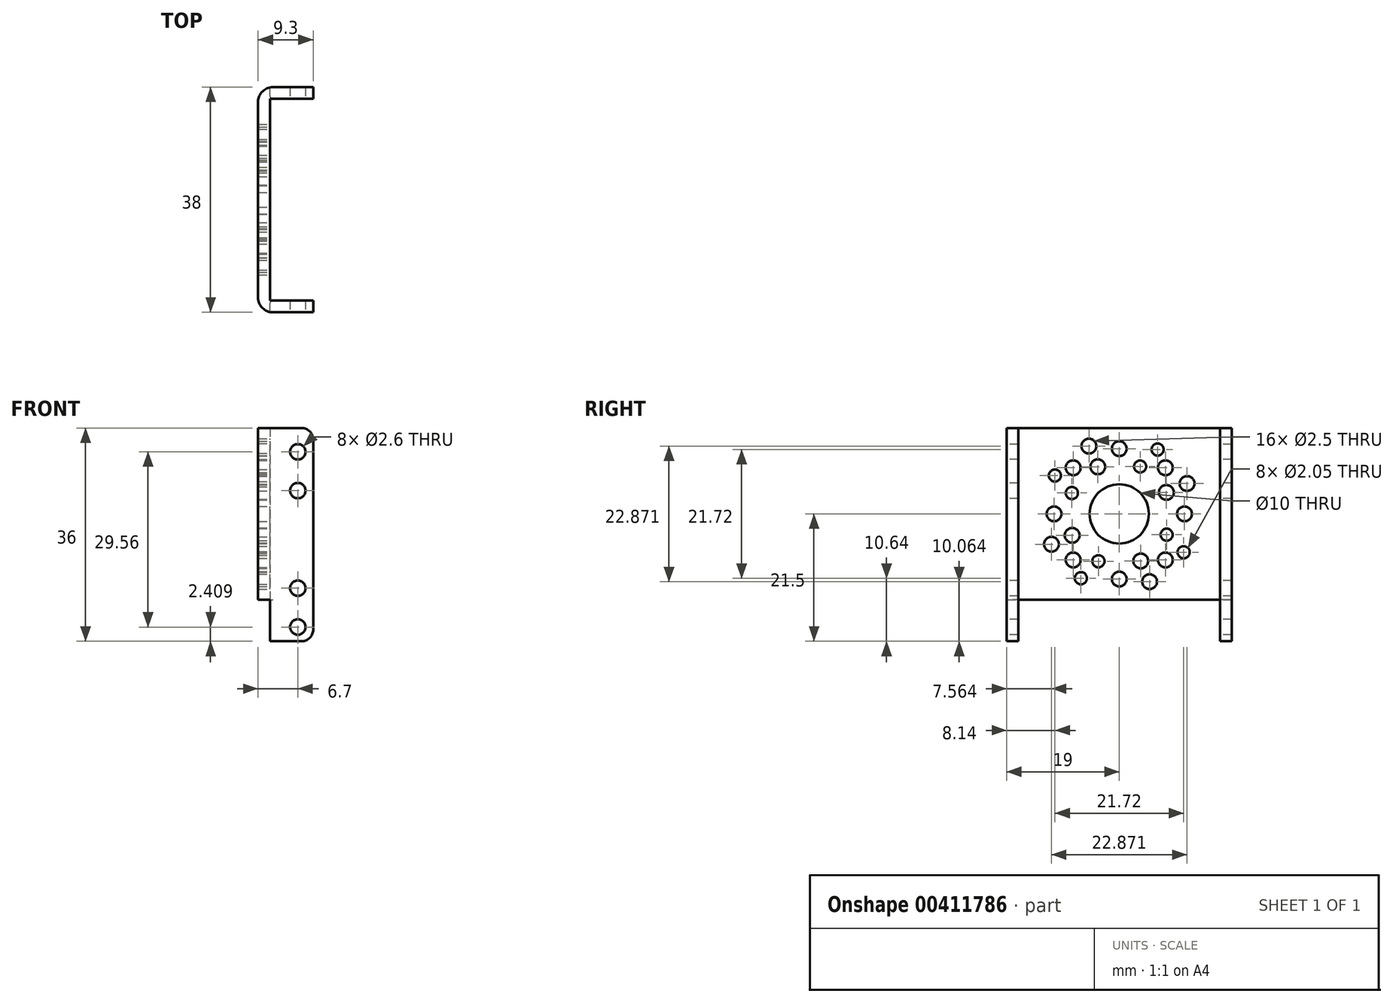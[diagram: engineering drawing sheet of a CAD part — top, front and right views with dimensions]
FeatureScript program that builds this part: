
annotation { "Feature Type Name" : "Feature", "Feature Type Description" : "" }
export const myFeature = defineFeature(function(context is Context, id is Id, definition is map)
    precondition{}
    {
        {
            var Q0;
            Q0=qCreatedBy(makeId("Right.planeOp"),FACE);
            var sketch = newSketch(context, id + "F0", { "sketchPlane" : qUnion([Q0])});
            skLineSegment(sketch, "E0.bottom", {"start": v(-19, 14.5) * mm, "end": v(19, 14.5) * mm});
            skLineSegment(sketch, "E0.top", {"start": v(-19, -14.5) * mm, "end": v(19, -14.5) * mm});
            skLineSegment(sketch, "E0.left", {"start": v(-19, 14.5) * mm, "end": v(-19, -14.5) * mm});
            skLineSegment(sketch, "E0.right", {"start": v(19, 14.5) * mm, "end": v(19, -14.5) * mm});
            skPoint(sketch, "E0.middle", {"position": v(0, 0) * mm});
            skSolve(sketch);
        }
        {
            var Q0;
            Q0=qSketchRegion(id+"F0",true);
            extrude(context, id + "F1", {"entities" : qUnion([Q0]), "depth" : 2 * mm});
        }
        {
            var Q0;
            Q0=makeQuery(id+"F1.opExtrude","CAP_FACE",FACE,{"disambiguationData":[OSD([sQuery(id+"F0.wireOp",EDGE,"E0.bottom"),sQuery(id+"F0.wireOp",EDGE,"E0.top"),sQuery(id+"F0.wireOp",EDGE,"E0.left"),sQuery(id+"F0.wireOp",EDGE,"E0.right")])],"isStart":false});
            var sketch = newSketch(context, id + "F2", { "sketchPlane" : qUnion([Q0])});
            skLineSegment(sketch, "E1.bottom", {"start": v(19, 14.5) * mm, "end": v(17, 14.5) * mm});
            skLineSegment(sketch, "E1.top", {"start": v(19, -21.5) * mm, "end": v(17, -21.5) * mm});
            skLineSegment(sketch, "E1.left", {"start": v(19, 14.5) * mm, "end": v(19, -21.5) * mm});
            skLineSegment(sketch, "E1.right", {"start": v(17, 14.5) * mm, "end": v(17, -21.5) * mm});
            skLineSegment(sketch, "E2.MirrorCS", {"start": v(-19, 14.5) * mm, "end": v(-19, -21.5) * mm});
            skLineSegment(sketch, "E3.MirrorCS", {"start": v(-19, 14.5) * mm, "end": v(-17, 14.5) * mm});
            skLineSegment(sketch, "E4.MirrorCS", {"start": v(-17, 14.5) * mm, "end": v(-17, -21.5) * mm});
            skLineSegment(sketch, "E5.MirrorCS", {"start": v(-19, -21.5) * mm, "end": v(-17, -21.5) * mm});
            skSolve(sketch);
        }
        {
            var Q0;
            Q0=qSketchRegion(id+"F2",true);
            extrude(context, id + "F3", {"entities" : qUnion([Q0]), "operationType" : NewBodyOperationType.ADD, "depth" : 7.3 * mm});
        }
        {
            var Q0;
            Q0=makeQuery(id+"F3.opExtrude","CAP_EDGE",EDGE,{"disambiguationData":[OSD([sQuery(id+"F2.wireOp",EDGE,"E5.MirrorCS")])],"isStart":false});
            var Q1;
            Q1=makeQuery(id+"F3.opExtrude","CAP_EDGE",EDGE,{"disambiguationData":[OSD([sQuery(id+"F2.wireOp",EDGE,"E1.top")])],"isStart":false});
            var Q2;
            Q2=makeQuery(id+"F3.opExtrude","CAP_EDGE",EDGE,{"disambiguationData":[OSD([sQuery(id+"F2.wireOp",EDGE,"E1.bottom")])],"isStart":false});
            var Q3;
            Q3=makeQuery(id+"F3.opExtrude","CAP_EDGE",EDGE,{"disambiguationData":[OSD([sQuery(id+"F2.wireOp",EDGE,"E3.MirrorCS")])],"isStart":false});
            fillet(context, id + "F4", {"entities" : qUnion([Q0, Q1, Q2, Q3]), "radius" : 2 * mm, "tangentPropagation" : true, "allowEdgeOverflow" : false});
        }
        {
            var Q0;
            {var subQ0=sQuery(id+"F2.wireOp",EDGE,"E4.MirrorCS");Q0=makeQuery(id+"F3.boolean.opBoolean","SPLIT",EDGE,{"disambiguationData":[topologyDisambiguationEdgeConnected([makeQuery(id+"F1.opExtrude","CAP_FACE",FACE,{"disambiguationData":[OSD([sQuery(id+"F0.wireOp",EDGE,"E0.bottom"),sQuery(id+"F0.wireOp",EDGE,"E0.top"),sQuery(id+"F0.wireOp",EDGE,"E0.left"),sQuery(id+"F0.wireOp",EDGE,"E0.right")])],"isStart":false})])],"derivedFrom":makeQuery(id+"F3.opExtrude","CAP_EDGE",EDGE,{"disambiguationData":[OSD([subQ0])],"isStart":true})});}
            var Q1;
            {var subQ0=sQuery(id+"F2.wireOp",EDGE,"E1.right");Q1=makeQuery(id+"F3.boolean.opBoolean","SPLIT",EDGE,{"disambiguationData":[topologyDisambiguationEdgeConnected([makeQuery(id+"F1.opExtrude","CAP_FACE",FACE,{"disambiguationData":[OSD([sQuery(id+"F0.wireOp",EDGE,"E0.bottom"),sQuery(id+"F0.wireOp",EDGE,"E0.top"),sQuery(id+"F0.wireOp",EDGE,"E0.left"),sQuery(id+"F0.wireOp",EDGE,"E0.right")])],"isStart":false})])],"derivedFrom":makeQuery(id+"F3.opExtrude","CAP_EDGE",EDGE,{"disambiguationData":[OSD([subQ0])],"isStart":true})});}
            fillet(context, id + "F5", {"entities" : qUnion([Q0, Q1]), "radius" : 0.5 * mm, "tangentPropagation" : true, "allowEdgeOverflow" : false});
        }
        {
            var Q0;
            Q0=makeQuery(id+"F1.opExtrude","CAP_EDGE",EDGE,{"disambiguationData":[OSD([sQuery(id+"F0.wireOp",EDGE,"E0.left")])],"isStart":true});
            var Q1;
            Q1=makeQuery(id+"F1.opExtrude","CAP_EDGE",EDGE,{"disambiguationData":[OSD([sQuery(id+"F0.wireOp",EDGE,"E0.right")])],"isStart":true});
            fillet(context, id + "F6", {"entities" : qUnion([Q0, Q1]), "radius" : 2.5 * mm, "tangentPropagation" : true, "allowEdgeOverflow" : false});
        }
        {
            var Q0;
            Q0=makeQuery(id+"F1.opExtrude","CAP_FACE",FACE,{"disambiguationData":[OSD([sQuery(id+"F0.wireOp",EDGE,"E0.bottom"),sQuery(id+"F0.wireOp",EDGE,"E0.top"),sQuery(id+"F0.wireOp",EDGE,"E0.left"),sQuery(id+"F0.wireOp",EDGE,"E0.right")])],"isStart":false});
            var sketch = newSketch(context, id + "F7", { "sketchPlane" : qUnion([Q0])});
            skCircle(sketch, "E6", {"center": v(0, 0) * mm, "radius": 5 * mm});
            skCircle(sketch, "E7", {"center": v(0, -11) * mm, "radius": 1.25 * mm});
            skCircle(sketch, "E8.1.0", {"center": v(7.78, -7.78) * mm, "radius": 1.25 * mm});
            skCircle(sketch, "E8.2.0", {"center": v(11, 0) * mm, "radius": 1.25 * mm});
            skCircle(sketch, "E8.3.0", {"center": v(7.78, 7.78) * mm, "radius": 1.25 * mm});
            skCircle(sketch, "E8.4.0", {"center": v(0, 11) * mm, "radius": 1.25 * mm});
            skCircle(sketch, "E8.5.0", {"center": v(-7.78, 7.78) * mm, "radius": 1.25 * mm});
            skCircle(sketch, "E8.6.0", {"center": v(-11, 0) * mm, "radius": 1.25 * mm});
            skCircle(sketch, "E8.7.0", {"center": v(-7.78, -7.78) * mm, "radius": 1.25 * mm});
            skSolve(sketch);
        }
        {
            var Q0;
            Q0=qSketchRegion(id+"F7",true);
            extrude(context, id + "F8", {"entities" : qUnion([Q0]), "operationType" : NewBodyOperationType.REMOVE, "oppositeDirection" : true, "depth" : 25 * mm});
        }
        {
            var Q0;
            Q0=makeQuery(id+"F1.opExtrude","CAP_FACE",FACE,{"disambiguationData":[OSD([sQuery(id+"F0.wireOp",EDGE,"E0.bottom"),sQuery(id+"F0.wireOp",EDGE,"E0.top"),sQuery(id+"F0.wireOp",EDGE,"E0.left"),sQuery(id+"F0.wireOp",EDGE,"E0.right")])],"isStart":false});
            var sketch = newSketch(context, id + "F9", { "sketchPlane" : qUnion([Q0])});
            skCircle(sketch, "E9", {"center": v(-11.44, -5.12) * mm, "radius": 1.25 * mm});
            skCircle(sketch, "E10.1.0", {"center": v(5.12, -11.44) * mm, "radius": 1.25 * mm});
            skCircle(sketch, "E10.2.0", {"center": v(11.44, 5.12) * mm, "radius": 1.25 * mm});
            skCircle(sketch, "E10.3.0", {"center": v(-5.12, 11.44) * mm, "radius": 1.25 * mm});
            skPoint(sketch, "E10.center", {"position": v(0, 0) * mm});
            skSolve(sketch);
        }
        {
            var Q0;
            Q0=qSketchRegion(id+"F9",true);
            extrude(context, id + "F10", {"entities" : qUnion([Q0]), "operationType" : NewBodyOperationType.REMOVE, "oppositeDirection" : true, "depth" : 25 * mm});
        }
        {
            var Q0;
            Q0=makeQuery(id+"F1.opExtrude","CAP_FACE",FACE,{"disambiguationData":[OSD([sQuery(id+"F0.wireOp",EDGE,"E0.bottom"),sQuery(id+"F0.wireOp",EDGE,"E0.top"),sQuery(id+"F0.wireOp",EDGE,"E0.left"),sQuery(id+"F0.wireOp",EDGE,"E0.right")])],"isStart":false});
            var sketch = newSketch(context, id + "F11", { "sketchPlane" : qUnion([Q0])});
            skCircle(sketch, "E11", {"center": v(-8, 3.52) * mm, "radius": 1.02 * mm});
            skCircle(sketch, "E12.1.0", {"center": v(-3.52, -8) * mm, "radius": 1.02 * mm});
            skCircle(sketch, "E12.2.0", {"center": v(8, -3.52) * mm, "radius": 1.02 * mm});
            skCircle(sketch, "E12.3.0", {"center": v(3.52, 8) * mm, "radius": 1.02 * mm});
            skPoint(sketch, "E12.center", {"position": v(0, 0) * mm});
            skSolve(sketch);
        }
        {
            var Q0;
            Q0=qSketchRegion(id+"F11",true);
            extrude(context, id + "F12", {"entities" : qUnion([Q0]), "operationType" : NewBodyOperationType.REMOVE, "oppositeDirection" : true, "depth" : 25 * mm});
        }
        {
            var Q0;
            Q0=makeQuery(id+"F1.opExtrude","CAP_FACE",FACE,{"disambiguationData":[OSD([sQuery(id+"F0.wireOp",EDGE,"E0.bottom"),sQuery(id+"F0.wireOp",EDGE,"E0.top"),sQuery(id+"F0.wireOp",EDGE,"E0.left"),sQuery(id+"F0.wireOp",EDGE,"E0.right")])],"isStart":false});
            var sketch = newSketch(context, id + "F13", { "sketchPlane" : qUnion([Q0])});
            skCircle(sketch, "E13", {"center": v(-7.95, -3.62) * mm, "radius": 1.25 * mm});
            skCircle(sketch, "E14.1.0", {"center": v(3.62, -7.95) * mm, "radius": 1.25 * mm});
            skCircle(sketch, "E14.2.0", {"center": v(7.95, 3.62) * mm, "radius": 1.25 * mm});
            skCircle(sketch, "E14.3.0", {"center": v(-3.62, 7.95) * mm, "radius": 1.25 * mm});
            skPoint(sketch, "E14.center", {"position": v(0, 0) * mm});
            skSolve(sketch);
        }
        {
            var Q0;
            Q0=qSketchRegion(id+"F13",true);
            extrude(context, id + "F14", {"entities" : qUnion([Q0]), "operationType" : NewBodyOperationType.REMOVE, "oppositeDirection" : true, "depth" : 25 * mm});
        }
        {
            var Q0;
            Q0=makeQuery(id+"F1.opExtrude","CAP_FACE",FACE,{"disambiguationData":[OSD([sQuery(id+"F0.wireOp",EDGE,"E0.bottom"),sQuery(id+"F0.wireOp",EDGE,"E0.top"),sQuery(id+"F0.wireOp",EDGE,"E0.left"),sQuery(id+"F0.wireOp",EDGE,"E0.right")])],"isStart":false});
            var sketch = newSketch(context, id + "F15", { "sketchPlane" : qUnion([Q0])});
            skCircle(sketch, "E15", {"center": v(-10.86, 6.47) * mm, "radius": 1.02 * mm});
            skCircle(sketch, "E16.1.0", {"center": v(-6.47, -10.86) * mm, "radius": 1.02 * mm});
            skCircle(sketch, "E16.2.0", {"center": v(10.86, -6.47) * mm, "radius": 1.02 * mm});
            skCircle(sketch, "E16.3.0", {"center": v(6.47, 10.86) * mm, "radius": 1.02 * mm});
            skPoint(sketch, "E16.center", {"position": v(0, 0) * mm});
            skSolve(sketch);
        }
        {
            var Q0;
            Q0=qSketchRegion(id+"F15",true);
            extrude(context, id + "F16", {"entities" : qUnion([Q0]), "operationType" : NewBodyOperationType.REMOVE, "oppositeDirection" : true, "depth" : 25 * mm});
        }
        {
            var Q0;
            Q0=makeQuery(id+"F3.boolean.opBoolean","MERGE",FACE,{"derivedFrom":[makeQuery(id+"F1.opExtrude","SWEPT_FACE",FACE,{"disambiguationData":[OSD([sQuery(id+"F0.wireOp",EDGE,"E0.left")])]}),makeQuery(id+"F3.opExtrude","SWEPT_FACE",FACE,{"disambiguationData":[OSD([sQuery(id+"F2.wireOp",EDGE,"E2.MirrorCS")])]})]});
            var sketch = newSketch(context, id + "F17", { "sketchPlane" : qUnion([Q0])});
            skCircle(sketch, "E17", {"center": v(6.7, 10.47) * mm, "radius": 1.3 * mm});
            skCircle(sketch, "E18", {"center": v(6.7, 3.92) * mm, "radius": 1.3 * mm});
            skCircle(sketch, "E19", {"center": v(6.7, -12.55) * mm, "radius": 1.3 * mm});
            skCircle(sketch, "E20", {"center": v(6.7, -19.1) * mm, "radius": 1.3 * mm});
            skSolve(sketch);
        }
        {
            var Q0;
            Q0=qSketchRegion(id+"F17",true);
            extrude(context, id + "F18", {"entities" : qUnion([Q0]), "operationType" : NewBodyOperationType.REMOVE, "oppositeDirection" : true, "depth" : 51.6 * mm});
        }
    });
